# Revit family: STI-100 IP телефон_RV17_LOD400
name_source: partatom
category: Телефонные устройства
revit_build: Autodesk Revit 2017 (Build: 20170118_1100(x64)
units: mm (PartAtom-declared; Revit-internal decimal feet)

## family parameters
Всегда вертикально = Нет
На основе рабочей плоскости = Нет
Общий = Нет
При загрузке вырезать с полостями = Нет
Размер круглого соединителя = Использовать диаметр
Сохранять ориентацию аннотаций = Нет
Тип детали = Нормальный
Точка расчета площади = Нет

## types (1)
- STI-100 IP телефон
    ADSK_URL страницы изделия = https://stilsoft.ru
    ADSK_Единица измерения = шт.
    ADSK_Завод-изготовитель = ООО «Основа Безопасности»
    ADSK_Количество = 1
    ADSK_Марка = СТВФ.431295.005-02
    ADSK_Масса = 0.51
    ADSK_Наименование = IP телефон STI-100
    ADSK_Размер_Высота = 51 мм
    ADSK_Размер_Длина = 195 мм
    ADSK_Размер_Ширина = 188 мм
    QoS = IEEE 802.1Q
IEEE 802.1Q и IEEE 802.1p
    QoS (1) = Diffserv (DSCP)/ToS
    d_короба = 20 мм
    Аудио кодеки = G.711a/u (64 Кбит/с)
    Аудио кодеки (1) = G.729A/B (8 Кбит/с)
    Аудио кодеки (2) = G.723.1; G.726-32; G.722
    Голосовые функции = Подавление пауз
    Голосовые функции (1) = Акустическое подавление эха. Обнаружение голосовой активности
    Голосовые функции (2) = Генерация фонового шума
    Голосовые функции (3) = Jitter-буфер
    Голосовые функции (4) = Передатчик DTMF
    Голосовые функции (5) = Маскирование потери пакетов
    Голосовые функции (6) = Поддержка HD Voice
    Диапазон рабочих температур, °C = от +5 до +50
    Дисплей = Цветной ЖК-дисплей с активной матрицей
    Дисплей (1) = Разрешение: 320 х 240 пикселей
    Дополнительные функции звонков = Удержание вызова / Возобновление вызова
    Дополнительные функции звонков (1) = Функция Call mute
    Дополнительные функции звонков (10) = Автоответ
    Дополнительные функции звонков (11) = Черный список
    Дополнительные функции звонков (12) = Limit list
    Дополнительные функции звонков (13) = Автоматическое завершение вызова
    Дополнительные функции звонков (14) = Автоматический повторный набор номера
    Дополнительные функции звонков (15) = Запрет определенных исходящих вызовов
    Дополнительные функции звонков (16) = Горячая линия
    Дополнительные функции звонков (17) = BLF/Presence
    Дополнительные функции звонков (18) = Интерком
    Дополнительные функции звонков (19) = Перехват вызова (Call Pickup)
    Дополнительные функции звонков (2) = Перевод вызова (несопровождаемый, сопровождаемый и с ранним сопровождением)
    Дополнительные функции звонков (20) = Action URL / Active URI
    Дополнительные функции звонков (3) = Перевод вызова (несопровождаемый, сопровождаемый и с ранним сопровождением)
    Дополнительные функции звонков (4) = Ожидание вызова
    Дополнительные функции звонков (5) = Индикация ожидания вызова
    Дополнительные функции звонков (6) = Трехсторонняя конференция
    Дополнительные функции звонков (7) = Анонимный вызов / блокировка анонимного вызова
    Дополнительные функции звонков (8) = Индикация ожидания сообщения
    Дополнительные функции звонков (9) = Функция «Не беспокоить»
    Клавиатура = 12 цифровых клавиш
    Клавиатура (1) = 11 функциональных клавиш
    Клавиатура (2) = 4 программируемые клавиши
    Клавиатура (4) = 4 клавиши для навигации
    Клавиатура (5) = 8 клавиш DSS
    Напряжение электропитания = 5В постоянного тока
    Напряжение электропитания (1) = по кабелю Ethernet (PoE) 802.3af (класс 1)
    Потребляемая мощность, не более, Вт = 1,3 (в режиме ожидания)
    Потребляемая мощность, не более, Вт (1) = 4,3 (в режиме разговора)
    Сетевой интерфейс = Порт WAN 10/100Base-TX для подключения к сети Интернет/PoE-коммутатору
    Сетевой интерфейс (1) = Порт LAN 10/100Base-TX для подключения к ПК
    Сетевой интерфейс (2) = Разъем для подключения гарнитуры
    Сетевой интерфейс (3) = Разъем для подключения модуля расширения
    Сигнальные, медиа и сетевые протоколы = SIP RFC 3261
    Сигнальные, медиа и сетевые протоколы (1) = SIP RFC 2327
    Сигнальные, медиа и сетевые протоколы (2) = RTP RFC 1889
    Сигнальные, медиа и сетевые протоколы (3) = Назначение IP-адреса: статический IP-адрес, DHCP и РРРоЕ
    Сигнальные, медиа и сетевые протоколы (4) = STUN, static port mapping (для NAT traversal)
    Сигнальные, медиа и сетевые протоколы (5) = SNTP
    Сигнальные, медиа и сетевые протоколы (6) = DNS и DNS SRV
    Сигнальные, медиа и сетевые протоколы (7) = TFTP/FTP/HTTP для автоконфигурирования
    Сигнальные, медиа и сетевые протоколы (8) = IP/TCP/UDP/ARP/ICMP
